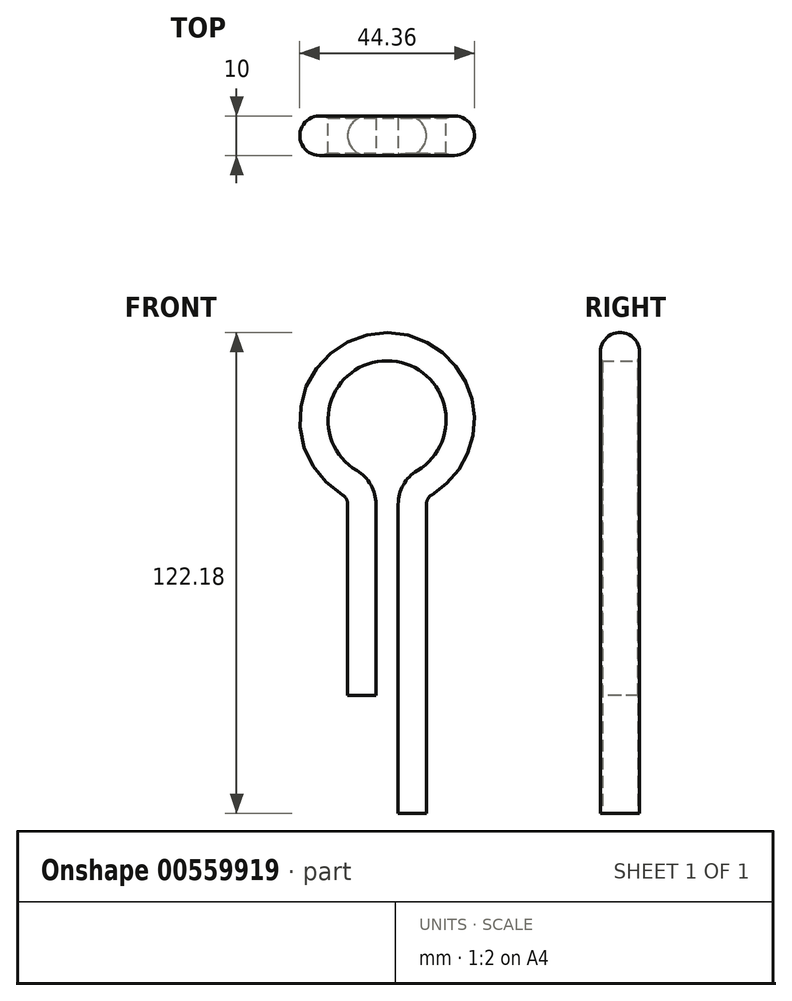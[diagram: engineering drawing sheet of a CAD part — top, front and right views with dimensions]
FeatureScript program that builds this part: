
annotation { "Feature Type Name" : "Feature", "Feature Type Description" : "" }
export const myFeature = defineFeature(function(context is Context, id is Id, definition is map)
    precondition{}
    {
        {
            var Q0;
            Q0=qCreatedBy(makeId("Top.planeOp"),FACE);
            var sketch = newSketch(context, id + "F0", { "sketchPlane" : qUnion([Q0])});
            skLineSegment(sketch, "E0", {"start": v(0, 4.5) * mm, "end": v(0, -4.5) * mm});
            skArc(sketch, "E1", {"start": v(0, 4.5) * mm, "mid": v(-7.18, 0) * mm, "end": v(0, -4.5) * mm});
            skSolve(sketch);
        }
        {
            var Q0;
            Q0=qCreatedBy(makeId("Front.planeOp"),FACE);
            var sketch = newSketch(context, id + "F1", { "sketchPlane" : qUnion([Q0])});
            skLineSegment(sketch, "E2", {"start": v(0, 0) * mm, "end": v(0, 48.54) * mm});
            skLineSegment(sketch, "E3", {"start": v(2.82, 0) * mm, "end": v(2.82, 70) * mm, "construction": true});
            skCircle(sketch, "E4", {"center": v(2.82, 70) * mm, "radius": 15 * mm});
            skArc(sketch, "E5", {"start": v(10.51, 57.12) * mm, "mid": v(2.82, 85) * mm, "end": v(-4.87, 57.12) * mm});
            skLineSegment(sketch, "E6", {"start": v(5.64, 48.54) * mm, "end": v(5.64, -30) * mm});
            skPoint(sketch, "E7.visualSharp", {"position": v(0, 55.27) * mm});
            skArc(sketch, "E7.filletArc", {"start": v(0, 48.54) * mm, "mid": v(-1.3, 53.47) * mm, "end": v(-4.87, 57.12) * mm});
            skPoint(sketch, "E8.visualSharp", {"position": v(5.64, 55.27) * mm});
            skArc(sketch, "E8.filletArc", {"start": v(10.51, 57.12) * mm, "mid": v(6.94, 53.47) * mm, "end": v(5.64, 48.54) * mm});
            skSolve(sketch);
        }
        {
            var Q0;
            Q0=makeQuery(id+"F0.imprint","IMPRINT",FACE,{"disambiguationData":[TD([[makeQuery(id+"F0.imprint","IMPRINT",EDGE,{"derivedFrom":sQuery(id+"F0.wireOp",EDGE,"E0")}),-1.0]])]});
            var Q1;
            Q1=sQuery(id+"F1.wireOp",EDGE,"E2");
            var Q2;
            Q2=sQuery(id+"F1.wireOp",EDGE,"E7.filletArc");
            var Q3;
            Q3=sQuery(id+"F1.wireOp",EDGE,"E5");
            var Q4;
            Q4=sQuery(id+"F1.wireOp",EDGE,"E8.filletArc");
            var Q5;
            Q5=sQuery(id+"F1.wireOp",EDGE,"E6");
            sweep(context, id + "F2", {"profiles" : qUnion([Q0]), "path" : qUnion([Q1, Q2, Q3, Q4, Q5])});
        }
    });
